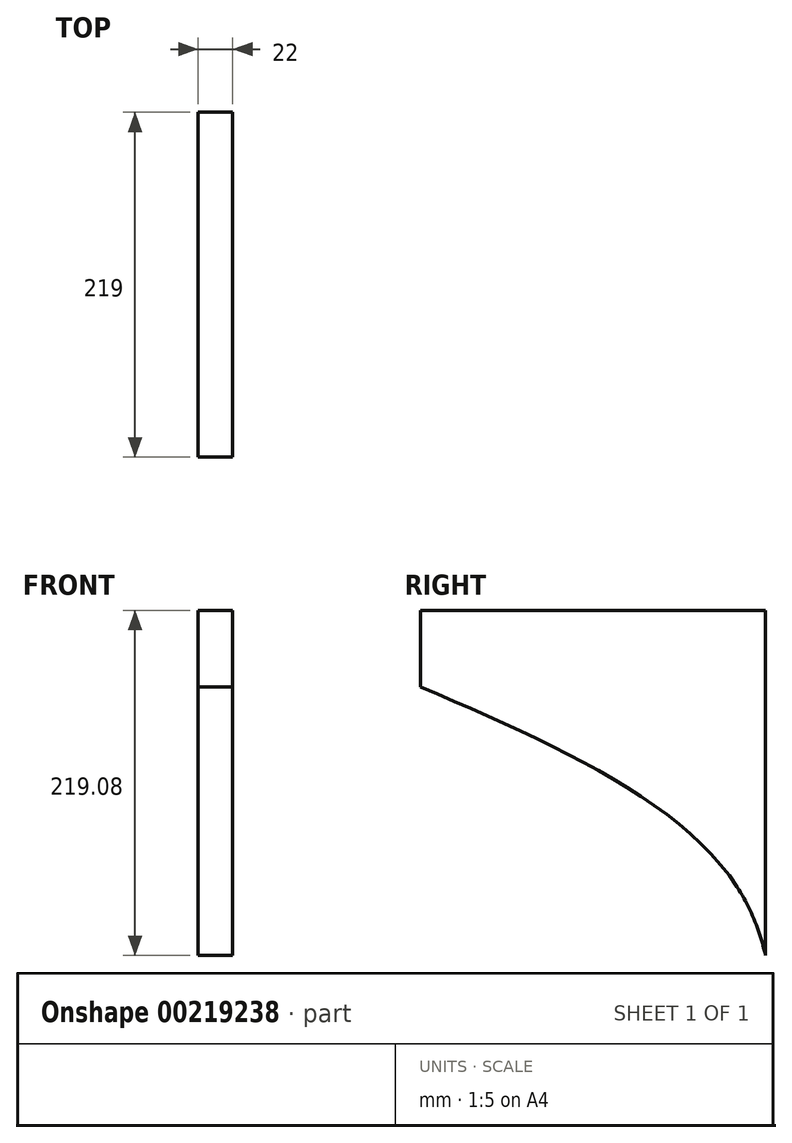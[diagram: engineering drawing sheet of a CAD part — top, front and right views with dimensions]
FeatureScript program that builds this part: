
annotation { "Feature Type Name" : "Feature", "Feature Type Description" : "" }
export const myFeature = defineFeature(function(context is Context, id is Id, definition is map)
    precondition{}
    {
        {
            var Q0;
            Q0=qCreatedBy(makeId("Right.planeOp"),FACE);
            var sketch = newSketch(context, id + "F0", { "sketchPlane" : qUnion([Q0])});
            skLineSegment(sketch, "E0.bottom", {"start": v(109.5, 217.03) * mm, "end": v(-109.5, 217.03) * mm});
            skLineSegment(sketch, "E0.top", {"start": v(109.5, -217.03) * mm, "end": v(-109.5, -217.03) * mm});
            skLineSegment(sketch, "E0.left", {"start": v(109.5, 217.03) * mm, "end": v(109.5, -17.53) * mm});
            skLineSegment(sketch, "E0.right", {"start": v(-109.5, 217.03) * mm, "end": v(-109.5, -217.03) * mm});
            skPoint(sketch, "E0.middle", {"position": v(0, 0) * mm});
            skPoint(sketch, "E1", {"position": v(-109.5, 209.03) * mm});
            skPoint(sketch, "E2", {"position": v(-109.5, -218.5) * mm});
            skPoint(sketch, "E3.positionSnap0", {"position": v(109.5, 0) * mm});
            skPoint(sketch, "E4", {"position": v(-109.5, -30) * mm});
            skPoint(sketch, "E5", {"position": v(-109.5, 168.5) * mm});
            skPoint(sketch, "E6", {"position": v(91.5, -28.53) * mm});
            skLineSegment(sketch, "E7", {"start": v(91.5, -28.53) * mm, "end": v(91.5, -98.53) * mm});
            skLineSegment(sketch, "E8", {"start": v(91.5, -28.53) * mm, "end": v(91.5, 41.47) * mm});
            skLineSegment(sketch, "E9.bottom", {"start": v(109.5, -17.53) * mm, "end": v(100.5, -17.53) * mm});
            skLineSegment(sketch, "E9.top", {"start": v(109.5, -39.53) * mm, "end": v(100.5, -39.53) * mm});
            skLineSegment(sketch, "E9.right", {"start": v(100.5, -17.53) * mm, "end": v(100.5, -39.53) * mm});
            skLineSegment(sketch, "E10.trimOffspring", {"start": v(109.5, -39.53) * mm, "end": v(109.5, -217.03) * mm});
            skFitSpline(sketch, "E11", {"points": [v(-109.5, 168.5) * mm, v(91.5, 41.47) * mm, v(91.5, -98.53) * mm, v(-109.5, -217.03) * mm], "startDerivative": vector(676.4, -289.83) * mm, "endDerivative": vector(-697.58, -221.33) * mm});
            skFitSpline(sketch, "E12.trimOffspring", {"points": [v(-109.5, 168.5) * mm, v(91.5, 41.47) * mm, v(91.5, -98.53) * mm, v(-109.5, -217.03) * mm], "startDerivative": vector(676.4, -289.83) * mm, "endDerivative": vector(-697.58, -221.33) * mm});
            skSolve(sketch);
        }
        {
            var Q0;
            {var subQ4=sQuery(id+"F0.wireOp",EDGE,"E0.bottom");Q0=makeQuery(id+"F0.imprint","IMPRINT",FACE,{"disambiguationData":[TD([[makeQuery(id+"F0.imprint","IMPRINT",EDGE,{"derivedFrom":subQ4}),1.0]])]});}
            extrude(context, id + "F1", {"entities" : qUnion([Q0]), "depth" : 22 * mm});
        }
    });
